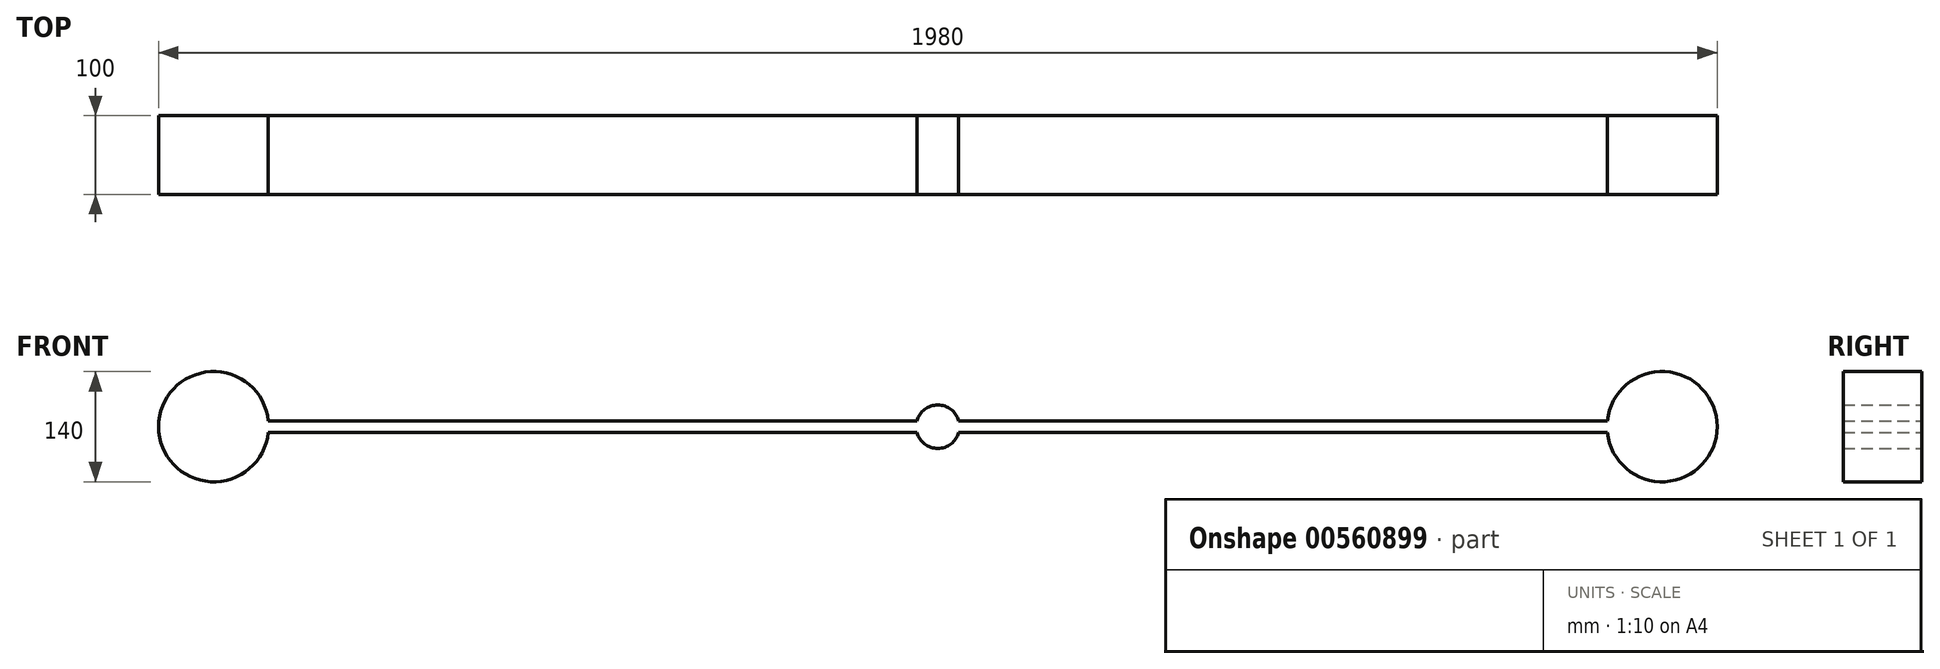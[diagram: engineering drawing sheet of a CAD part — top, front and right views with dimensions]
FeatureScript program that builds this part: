
annotation { "Feature Type Name" : "Feature", "Feature Type Description" : "" }
export const myFeature = defineFeature(function(context is Context, id is Id, definition is map)
    precondition{}
    {
        {
            var Q0;
            Q0=qCreatedBy(makeId("Front.planeOp"),FACE);
            var sketch = newSketch(context, id + "F0", { "sketchPlane" : qUnion([Q0])});
            skArc(sketch, "E0", {"start": v(-850.4, 7.5) * mm, "mid": v(-990, 0) * mm, "end": v(-850.4, -7.5) * mm});
            skArc(sketch, "E1", {"start": v(850.4, -7.5) * mm, "mid": v(990, 0) * mm, "end": v(850.4, 7.5) * mm});
            skLineSegment(sketch, "E2", {"start": v(-850.4, 7.5) * mm, "end": v(-26.53, 7.5) * mm});
            skLineSegment(sketch, "E3", {"start": v(-850.4, -7.5) * mm, "end": v(-26.53, -7.5) * mm});
            skLineSegment(sketch, "E4", {"start": v(0, -1087.3) * mm, "end": v(0, 7.5) * mm, "construction": true});
            skArc(sketch, "E5", {"start": v(-26.53, -7.5) * mm, "mid": v(0, -27.57) * mm, "end": v(26.53, -7.5) * mm});
            skArc(sketch, "E6.trimOffspring", {"start": v(26.53, 7.5) * mm, "mid": v(0, 27.57) * mm, "end": v(-26.53, 7.5) * mm});
            skLineSegment(sketch, "E7.trimOffspring", {"start": v(26.53, 7.5) * mm, "end": v(850.4, 7.5) * mm});
            skLineSegment(sketch, "E8.trimOffspring", {"start": v(26.53, -7.5) * mm, "end": v(850.4, -7.5) * mm});
            skSolve(sketch);
        }
        {
            var Q0;
            Q0=makeQuery(id+"F0.imprint","IMPRINT",FACE,{"disambiguationData":[TD([[makeQuery(id+"F0.imprint","IMPRINT",EDGE,{"derivedFrom":sQuery(id+"F0.wireOp",EDGE,"E0")}),1.0]])]});
            var Q1;
            Q1=makeQuery(id+"F0.imprint","IMPRINT",FACE,{"disambiguationData":[TD([[makeQuery(id+"F0.imprint","IMPRINT",EDGE,{"derivedFrom":sQuery(id+"F0.wireOp",EDGE,"E1")}),1.0]])]});
            extrude(context, id + "F1", {"entities" : qUnion([Q0, Q1]), "depth" : 100 * mm, "offsetDistance" : 25 * mm});
        }
    });
